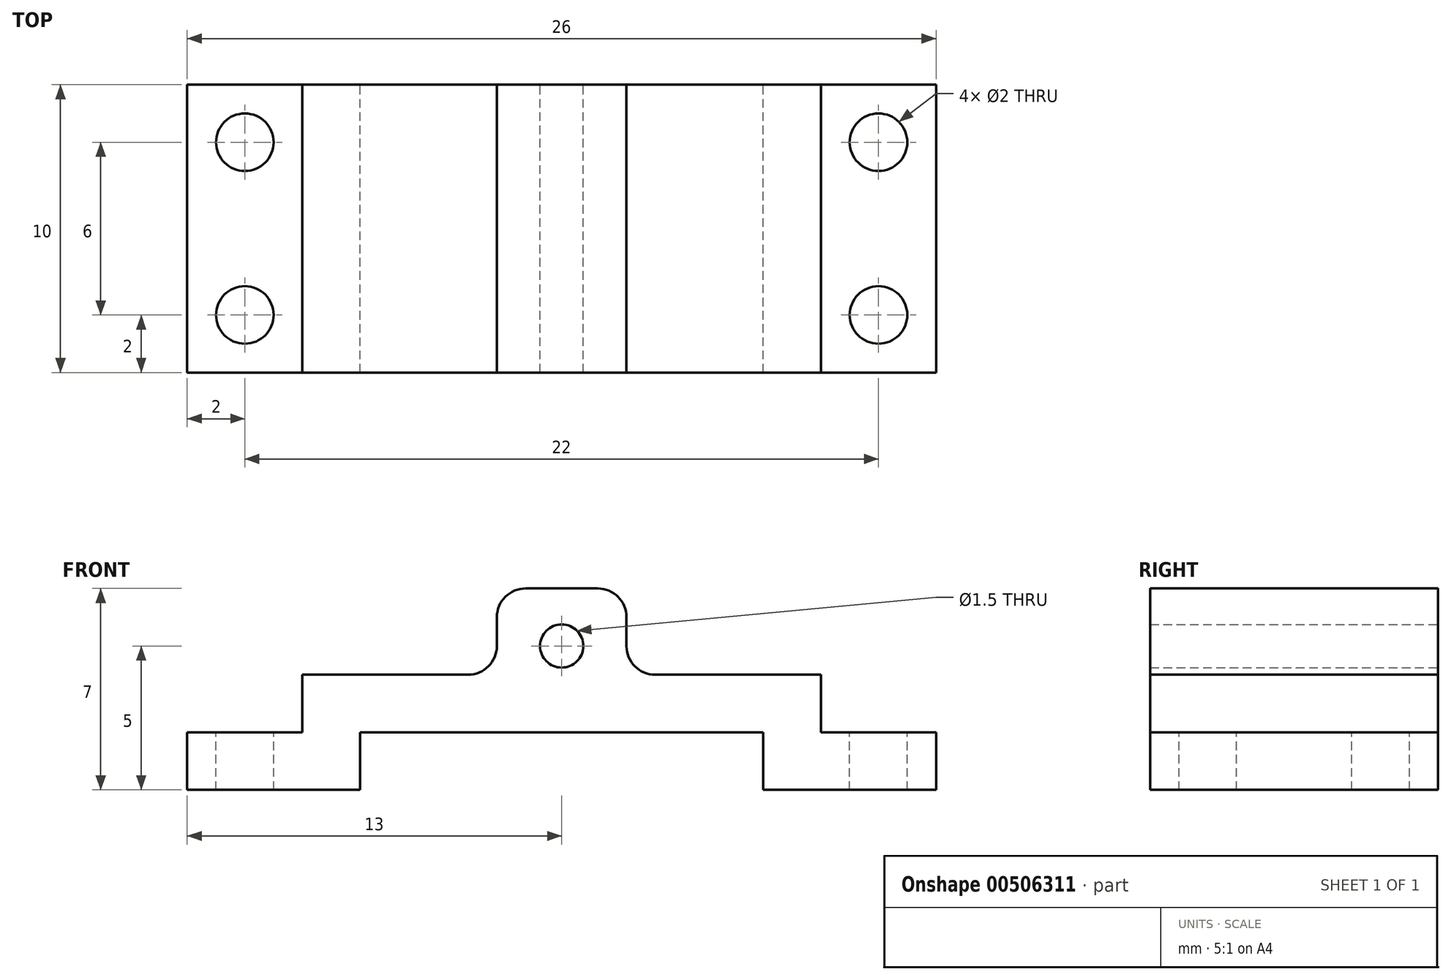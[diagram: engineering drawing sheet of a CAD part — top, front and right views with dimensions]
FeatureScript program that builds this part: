
annotation { "Feature Type Name" : "Feature", "Feature Type Description" : "" }
export const myFeature = defineFeature(function(context is Context, id is Id, definition is map)
    precondition{}
    {
        {
            var Q0;
            Q0=qCreatedBy(makeId("Front.planeOp"),FACE);
            var sketch = newSketch(context, id + "F0", { "sketchPlane" : qUnion([Q0])});
            skLineSegment(sketch, "E0.bottom", {"start": v(-13, 0) * mm, "end": v(13, 0) * mm});
            skLineSegment(sketch, "E0.top", {"start": v(-13, 4) * mm, "end": v(13, 4) * mm});
            skLineSegment(sketch, "E0.left", {"start": v(-13, 0) * mm, "end": v(-13, 4) * mm});
            skLineSegment(sketch, "E0.right", {"start": v(13, 0) * mm, "end": v(13, 4) * mm});
            skPoint(sketch, "E1", {"position": v(0, 4) * mm});
            skLineSegment(sketch, "E2.bottom", {"start": v(-7, 0) * mm, "end": v(7, 0) * mm});
            skLineSegment(sketch, "E2.top", {"start": v(-7, 2) * mm, "end": v(7, 2) * mm});
            skLineSegment(sketch, "E2.left", {"start": v(-7, 0) * mm, "end": v(-7, 2) * mm});
            skLineSegment(sketch, "E2.right", {"start": v(7, 0) * mm, "end": v(7, 2) * mm});
            skCircle(sketch, "E3", {"center": v(0, 5) * mm, "radius": 0.75 * mm});
            skLineSegment(sketch, "E4.bottom", {"start": v(-2.25, 4) * mm, "end": v(2.25, 4) * mm});
            skLineSegment(sketch, "E4.top", {"start": v(-2.25, 7) * mm, "end": v(2.25, 7) * mm});
            skLineSegment(sketch, "E4.left", {"start": v(-2.25, 4) * mm, "end": v(-2.25, 7) * mm});
            skLineSegment(sketch, "E4.right", {"start": v(2.25, 4) * mm, "end": v(2.25, 7) * mm});
            skSolve(sketch);
        }
        {
            var Q0;
            {var subQ3=sQuery(id+"F0.wireOp",EDGE,"E0.left");Q0=makeQuery(id+"F0.imprint","IMPRINT",FACE,{"disambiguationData":[TD([[makeQuery(id+"F0.imprint","IMPRINT",EDGE,{"derivedFrom":subQ3}),-1.0]])]});}
            var Q1;
            Q1=makeQuery(id+"F0.imprint","IMPRINT",FACE,{"disambiguationData":[TD([[makeQuery(id+"F0.imprint","IMPRINT",EDGE,{"derivedFrom":sQuery(id+"F0.wireOp",EDGE,"E3")}),-1.0]])]});
            extrude(context, id + "F1", {"entities" : qUnion([Q0, Q1]), "depth" : 10 * mm});
        }
        {
            var Q0;
            {var subQ0=sQuery(id+"F0.wireOp",EDGE,"E0.top");Q0=makeQuery(id+"F1.opExtrude","SWEPT_FACE",FACE,{"disambiguationData":[OSD([subQ0]),TDD([makeQuery(id+"F0.imprint","IMPRINT",EDGE,{"disambiguationData":[TD([[makeQuery(id+"F0.imprint","INTERSECT",VERTEX,{"derivedFrom":[subQ0,sQuery(id+"F0.wireOp",EDGE,"E0.left")]}),-1.0]])],"derivedFrom":subQ0})])]});}
            var sketch = newSketch(context, id + "F2", { "sketchPlane" : qUnion([Q0])});
            skCircle(sketch, "E5", {"center": v(-11, -2) * mm, "radius": 1 * mm});
            skCircle(sketch, "E6", {"center": v(-11, -8) * mm, "radius": 1 * mm});
            skSolve(sketch);
        }
        {
            var Q0;
            Q0=makeQuery(id+"F2.imprint","IMPRINT",FACE,{"disambiguationData":[TD([[makeQuery(id+"F2.imprint","IMPRINT",EDGE,{"derivedFrom":sQuery(id+"F2.wireOp",EDGE,"E5")}),1.0]])]});
            var Q1;
            Q1=makeQuery(id+"F2.imprint","IMPRINT",FACE,{"disambiguationData":[TD([[makeQuery(id+"F2.imprint","IMPRINT",EDGE,{"derivedFrom":sQuery(id+"F2.wireOp",EDGE,"E6")}),1.0]])]});
            extrude(context, id + "F3", {"entities" : qUnion([Q0, Q1]), "operationType" : NewBodyOperationType.REMOVE, "oppositeDirection" : true, "depth" : 4 * mm});
        }
        {
            var Q0;
            {var subQ0=sQuery(id+"F0.wireOp",EDGE,"E0.top");Q0=makeQuery(id+"F1.opExtrude","SWEPT_FACE",FACE,{"disambiguationData":[OSD([subQ0]),TDD([makeQuery(id+"F0.imprint","IMPRINT",EDGE,{"disambiguationData":[TD([[makeQuery(id+"F0.imprint","INTERSECT",VERTEX,{"derivedFrom":[subQ0,sQuery(id+"F0.wireOp",EDGE,"E0.right")]}),1.0]])],"derivedFrom":subQ0})])]});}
            var sketch = newSketch(context, id + "F4", { "sketchPlane" : qUnion([Q0])});
            skCircle(sketch, "E7", {"center": v(11, -2) * mm, "radius": 1 * mm});
            skCircle(sketch, "E8", {"center": v(11, -8) * mm, "radius": 1 * mm});
            skSolve(sketch);
        }
        {
            var Q0;
            Q0=makeQuery(id+"F4.imprint","IMPRINT",FACE,{"disambiguationData":[TD([[makeQuery(id+"F4.imprint","IMPRINT",EDGE,{"derivedFrom":sQuery(id+"F4.wireOp",EDGE,"E7")}),1.0]])]});
            var Q1;
            Q1=makeQuery(id+"F4.imprint","IMPRINT",FACE,{"disambiguationData":[TD([[makeQuery(id+"F4.imprint","IMPRINT",EDGE,{"derivedFrom":sQuery(id+"F4.wireOp",EDGE,"E8")}),1.0]])]});
            extrude(context, id + "F5", {"entities" : qUnion([Q0, Q1]), "operationType" : NewBodyOperationType.REMOVE, "oppositeDirection" : true, "depth" : 4 * mm});
        }
        {
            var Q0;
            {var subQ0=sQuery(id+"F0.wireOp",EDGE,"E0.top");Q0=makeQuery(id+"F1.opExtrude","SWEPT_FACE",FACE,{"disambiguationData":[OSD([subQ0]),TDD([makeQuery(id+"F0.imprint","IMPRINT",EDGE,{"disambiguationData":[TD([[makeQuery(id+"F0.imprint","INTERSECT",VERTEX,{"derivedFrom":[subQ0,sQuery(id+"F0.wireOp",EDGE,"E0.left")]}),-1.0]])],"derivedFrom":subQ0})])]});}
            var sketch = newSketch(context, id + "F6", { "sketchPlane" : qUnion([Q0])});
            skLineSegment(sketch, "E9.bottom", {"start": v(-13, 0) * mm, "end": v(-9, 0) * mm});
            skLineSegment(sketch, "E9.top", {"start": v(-13, -10) * mm, "end": v(-9, -10) * mm});
            skLineSegment(sketch, "E9.left", {"start": v(-13, 0) * mm, "end": v(-13, -10) * mm});
            skLineSegment(sketch, "E9.right", {"start": v(-9, 0) * mm, "end": v(-9, -10) * mm});
            skSolve(sketch);
        }
        {
            var Q0;
            Q0=makeQuery(id+"F6.imprint","IMPRINT",FACE,{"disambiguationData":[TD([[makeQuery(id+"F6.imprint","IMPRINT",EDGE,{"derivedFrom":sQuery(id+"F6.wireOp",EDGE,"E9.bottom")}),-1.0]])]});
            extrude(context, id + "F7", {"entities" : qUnion([Q0]), "operationType" : NewBodyOperationType.REMOVE, "oppositeDirection" : true, "depth" : 2 * mm});
        }
        {
            var Q0;
            {var subQ0=sQuery(id+"F0.wireOp",EDGE,"E0.top");Q0=makeQuery(id+"F1.opExtrude","SWEPT_FACE",FACE,{"disambiguationData":[OSD([subQ0]),TDD([makeQuery(id+"F0.imprint","IMPRINT",EDGE,{"disambiguationData":[TD([[makeQuery(id+"F0.imprint","INTERSECT",VERTEX,{"derivedFrom":[subQ0,sQuery(id+"F0.wireOp",EDGE,"E0.right")]}),1.0]])],"derivedFrom":subQ0})])]});}
            var sketch = newSketch(context, id + "F8", { "sketchPlane" : qUnion([Q0])});
            skLineSegment(sketch, "E10.bottom", {"start": v(13, -10) * mm, "end": v(9, -10) * mm});
            skLineSegment(sketch, "E10.top", {"start": v(13, 0) * mm, "end": v(9, 0) * mm});
            skLineSegment(sketch, "E10.left", {"start": v(13, -10) * mm, "end": v(13, 0) * mm});
            skLineSegment(sketch, "E10.right", {"start": v(9, -10) * mm, "end": v(9, 0) * mm});
            skSolve(sketch);
        }
        {
            var Q0;
            Q0=makeQuery(id+"F8.imprint","IMPRINT",FACE,{"disambiguationData":[TD([[makeQuery(id+"F8.imprint","IMPRINT",EDGE,{"derivedFrom":sQuery(id+"F8.wireOp",EDGE,"E10.bottom")}),1.0]])]});
            extrude(context, id + "F9", {"entities" : qUnion([Q0]), "operationType" : NewBodyOperationType.REMOVE, "oppositeDirection" : true, "depth" : 2 * mm});
        }
        {
            var Q0;
            Q0=makeQuery(id+"F7.boolean.opBoolean","COPY",EDGE,{"derivedFrom":makeQuery(id+"F7.opExtrude","CAP_EDGE",EDGE,{"disambiguationData":[OSD([sQuery(id+"F6.wireOp",EDGE,"E9.right")])],"isStart":true})});
            var Q1;
            Q1=makeQuery(id+"F1.opExtrude","SWEPT_EDGE",EDGE,{"disambiguationData":[OSD([sQuery(id+"F0.wireOp",EDGE,"E4.top"),sQuery(id+"F0.wireOp",EDGE,"E4.left")])]});
            var Q2;
            Q2=makeQuery(id+"F1.opExtrude","SWEPT_EDGE",EDGE,{"disambiguationData":[OSD([sQuery(id+"F0.wireOp",EDGE,"E0.top"),sQuery(id+"F0.wireOp",EDGE,"E4.bottom"),sQuery(id+"F0.wireOp",EDGE,"E4.left")])]});
            var Q3;
            Q3=makeQuery(id+"F1.opExtrude","SWEPT_EDGE",EDGE,{"disambiguationData":[OSD([sQuery(id+"F0.wireOp",EDGE,"E4.top"),sQuery(id+"F0.wireOp",EDGE,"E4.right")])]});
            var Q4;
            Q4=makeQuery(id+"F1.opExtrude","SWEPT_EDGE",EDGE,{"disambiguationData":[OSD([sQuery(id+"F0.wireOp",EDGE,"E0.top"),sQuery(id+"F0.wireOp",EDGE,"E4.bottom"),sQuery(id+"F0.wireOp",EDGE,"E4.right")])]});
            var Q5;
            Q5=makeQuery(id+"F9.boolean.opBoolean","COPY",EDGE,{"derivedFrom":makeQuery(id+"F9.opExtrude","CAP_EDGE",EDGE,{"disambiguationData":[OSD([sQuery(id+"F8.wireOp",EDGE,"E10.right")])],"isStart":true})});
            var Q6;
            Q6=makeQuery(id+"F7.boolean.opBoolean","COPY",EDGE,{"derivedFrom":makeQuery(id+"F7.opExtrude","CAP_EDGE",EDGE,{"disambiguationData":[OSD([sQuery(id+"F6.wireOp",EDGE,"E9.left")])],"isStart":false})});
            var Q7;
            Q7=makeQuery(id+"F9.boolean.opBoolean","COPY",EDGE,{"derivedFrom":makeQuery(id+"F9.opExtrude","CAP_EDGE",EDGE,{"disambiguationData":[OSD([sQuery(id+"F8.wireOp",EDGE,"E10.left")])],"isStart":false})});
            fillet(context, id + "F10", {"entities" : qUnion([Q0, Q1, Q2, Q3, Q4, Q5, Q6, Q7]), "radius" : 1 * mm, "tangentPropagation" : true, "allowEdgeOverflow" : false});
        }
    });
